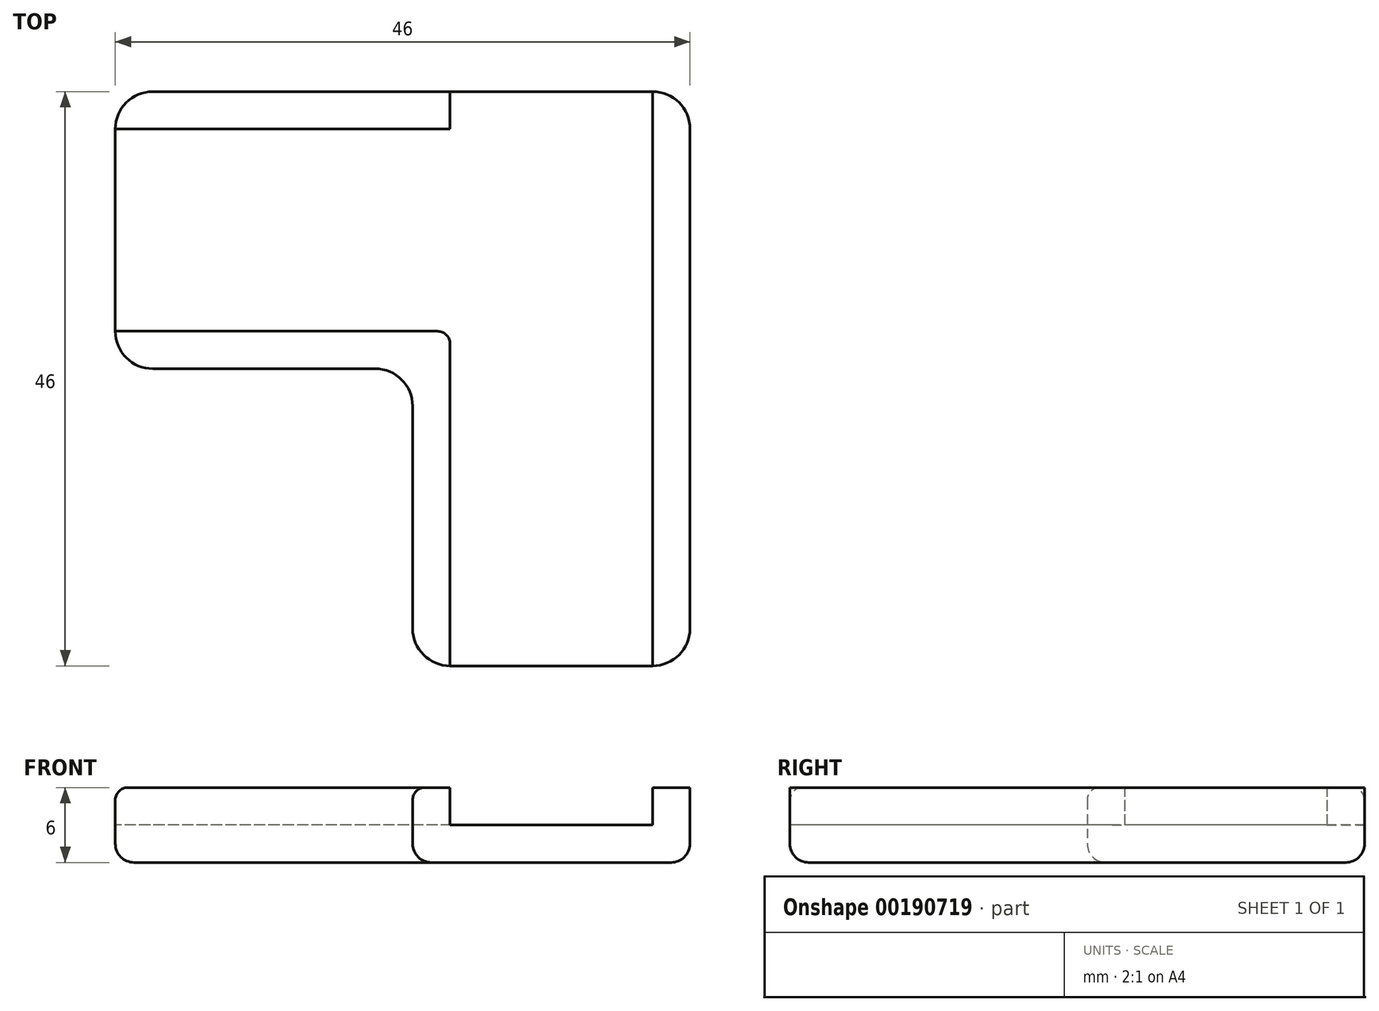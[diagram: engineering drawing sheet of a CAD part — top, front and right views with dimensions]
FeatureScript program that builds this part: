
annotation { "Feature Type Name" : "Feature", "Feature Type Description" : "" }
export const myFeature = defineFeature(function(context is Context, id is Id, definition is map)
    precondition{}
    {
        {
            var Q0;
            Q0=qCreatedBy(makeId("Top.planeOp"),FACE);
            var sketch = newSketch(context, id + "F0", { "sketchPlane" : qUnion([Q0])});
            skLineSegment(sketch, "E0.bottom", {"start": v(0, 0) * mm, "end": v(-40, 0) * mm, "construction": true});
            skLineSegment(sketch, "E0.top", {"start": v(-16.2, -16.2) * mm, "end": v(-40, -16.2) * mm, "construction": true});
            skLineSegment(sketch, "E0.left", {"start": v(0, 0) * mm, "end": v(0, -16.2) * mm, "construction": true});
            skLineSegment(sketch, "E0.right", {"start": v(-40, 0) * mm, "end": v(-40, -16.2) * mm, "construction": true});
            skLineSegment(sketch, "E1.bottom", {"start": v(0, 0) * mm, "end": v(-16.2, 0) * mm, "construction": true});
            skLineSegment(sketch, "E1.top", {"start": v(0, -40) * mm, "end": v(-16.2, -40) * mm, "construction": true});
            skLineSegment(sketch, "E1.left", {"start": v(0, 0) * mm, "end": v(0, -40) * mm, "construction": true});
            skLineSegment(sketch, "E1.right", {"start": v(-16.2, -16.2) * mm, "end": v(-16.2, -40) * mm, "construction": true});
            skLineSegment(sketch, "E2.0", {"start": v(3, 0) * mm, "end": v(3, -40) * mm});
            skLineSegment(sketch, "E2.1", {"start": v(-43, 0) * mm, "end": v(-43, -16.2) * mm});
            skLineSegment(sketch, "E2.2", {"start": v(-22.2, -19.2) * mm, "end": v(-40, -19.2) * mm});
            skLineSegment(sketch, "E2.3", {"start": v(0, 3) * mm, "end": v(-40, 3) * mm});
            skLineSegment(sketch, "E2.4", {"start": v(-19.2, -22.2) * mm, "end": v(-19.2, -40) * mm});
            skLineSegment(sketch, "E2.5", {"start": v(0, -43) * mm, "end": v(-16.2, -43) * mm});
            skPoint(sketch, "E3.visualSharp", {"position": v(-43, 3) * mm});
            skArc(sketch, "E3.filletArc", {"start": v(-40, 3) * mm, "mid": v(-42.12, 2.12) * mm, "end": v(-43, 0) * mm});
            skPoint(sketch, "E4.visualSharp", {"position": v(3, 3) * mm});
            skArc(sketch, "E4.filletArc", {"start": v(3, 0) * mm, "mid": v(2.12, 2.12) * mm, "end": v(0, 3) * mm});
            skPoint(sketch, "E5.visualSharp", {"position": v(3, -43) * mm});
            skArc(sketch, "E5.filletArc", {"start": v(0, -43) * mm, "mid": v(2.12, -42.12) * mm, "end": v(3, -40) * mm});
            skPoint(sketch, "E6.visualSharp", {"position": v(-19.2, -43) * mm});
            skArc(sketch, "E6.filletArc", {"start": v(-19.2, -40) * mm, "mid": v(-18.32, -42.12) * mm, "end": v(-16.2, -43) * mm});
            skPoint(sketch, "E7.visualSharp", {"position": v(-43, -19.2) * mm});
            skArc(sketch, "E7.filletArc", {"start": v(-43, -16.2) * mm, "mid": v(-42.12, -18.32) * mm, "end": v(-40, -19.2) * mm});
            skPoint(sketch, "E8.visualSharp", {"position": v(-19.2, -19.2) * mm});
            skArc(sketch, "E8.filletArc", {"start": v(-19.2, -22.2) * mm, "mid": v(-20.08, -20.08) * mm, "end": v(-22.2, -19.2) * mm});
            skSolve(sketch);
        }
        {
            var Q0;
            Q0=makeQuery(id+"F0.imprint","IMPRINT",FACE,{"disambiguationData":[TD([[makeQuery(id+"F0.imprint","IMPRINT",EDGE,{"derivedFrom":sQuery(id+"F0.wireOp",EDGE,"E2.0")}),-1.0]])]});
            extrude(context, id + "F1", {"entities" : qUnion([Q0]), "depth" : 6 * mm, "symmetric" : true});
        }
        {
            var Q0;
            Q0=qCreatedBy(makeId("Top.planeOp"),FACE);
            var sketch = newSketch(context, id + "F2", { "sketchPlane" : qUnion([Q0])});
            skLineSegment(sketch, "E9.0", {"start": v(-16.2, 0) * mm, "end": v(-43, 0) * mm});
            skLineSegment(sketch, "E9.1", {"start": v(-16.2, -16.2) * mm, "end": v(-43, -16.2) * mm});
            skLineSegment(sketch, "E9.2", {"start": v(0, 0) * mm, "end": v(0, -16.2) * mm});
            skLineSegment(sketch, "E9.6", {"start": v(0, 3) * mm, "end": v(0, -43) * mm});
            skLineSegment(sketch, "E9.7", {"start": v(-16.2, -16.2) * mm, "end": v(-16.2, -43) * mm});
            skLineSegment(sketch, "E9.9", {"start": v(-43, 0) * mm, "end": v(-43, -16.2) * mm});
            skLineSegment(sketch, "E9.10", {"start": v(-22.2, -19.2) * mm, "end": v(-40, -19.2) * mm});
            skPoint(sketch, "E9.11.end.orphan", {"position": v(-40, 3) * mm});
            skPoint(sketch, "E9.11.start.orphan", {"position": v(0, 3) * mm});
            skPoint(sketch, "E9.8.end.orphan", {"position": v(3, -40) * mm});
            skPoint(sketch, "E9.8.start.orphan", {"position": v(3, 0) * mm});
            skPoint(sketch, "E9.13.end.orphan", {"position": v(-16.2, -43) * mm});
            skPoint(sketch, "E9.13.start.orphan", {"position": v(0, -43) * mm});
            skPoint(sketch, "E9.12.end.orphan", {"position": v(-19.2, -40) * mm});
            skPoint(sketch, "E9.12.start.orphan", {"position": v(-19.2, -22.2) * mm});
            skPoint(sketch, "E9.3.end.orphan", {"position": v(-40, -16.2) * mm});
            skPoint(sketch, "E9.3.start.orphan", {"position": v(-40, 0) * mm});
            skPoint(sketch, "E9.5.end.orphan", {"position": v(-16.2, -40) * mm});
            skPoint(sketch, "E9.5.start.orphan", {"position": v(0, -40) * mm});
            skLineSegment(sketch, "E10.0", {"start": v(0, -43) * mm, "end": v(-16.2, -43) * mm, "construction": true});
            skPoint(sketch, "E11.orphan", {"position": v(-43, 0) * mm});
            skPoint(sketch, "E12.orphan", {"position": v(-43, -16.2) * mm});
            skLineSegment(sketch, "E13", {"start": v(-16.2, -43) * mm, "end": v(0, -43) * mm});
            skPoint(sketch, "E9.4.end.orphan", {"position": v(-16.2, 0) * mm});
            skPoint(sketch, "E9.4.start.orphan", {"position": v(0, 0) * mm});
            skLineSegment(sketch, "E14", {"start": v(-16.2, 0) * mm, "end": v(-16.2, 3) * mm});
            skLineSegment(sketch, "E15", {"start": v(0, 3) * mm, "end": v(-16.2, 3) * mm});
            skSolve(sketch);
        }
        {
            var Q0;
            Q0 = qSketchRegion(id + "F2", true);
            extrude(context, id + "F3", {"entities" : qUnion([Q0]), "operationType" : NewBodyOperationType.REMOVE, "depth" : 4 * mm});
        }
        {
            var Q0;
            Q0=makeQuery(id+"F1.opExtrude","CAP_FACE",FACE,{"disambiguationData":[OSD([sQuery(id+"F0.wireOp",EDGE,"E2.0"),sQuery(id+"F0.wireOp",EDGE,"E2.1"),sQuery(id+"F0.wireOp",EDGE,"E2.2"),sQuery(id+"F0.wireOp",EDGE,"E2.3"),sQuery(id+"F0.wireOp",EDGE,"E2.4"),sQuery(id+"F0.wireOp",EDGE,"E2.5"),sQuery(id+"F0.wireOp",EDGE,"E3.filletArc"),sQuery(id+"F0.wireOp",EDGE,"E4.filletArc"),sQuery(id+"F0.wireOp",EDGE,"E5.filletArc"),sQuery(id+"F0.wireOp",EDGE,"E6.filletArc"),sQuery(id+"F0.wireOp",EDGE,"E7.filletArc"),sQuery(id+"F0.wireOp",EDGE,"E8.filletArc")])],"isStart":true});
            fillet(context, id + "F4", {"entities" : qUnion([Q0]), "radius" : 1.5 * mm, "tangentPropagation" : true, "allowEdgeOverflow" : false});
        }
        {
            var Q0;
            Q0=makeQuery(id+"F1.opExtrude","CAP_EDGE",EDGE,{"disambiguationData":[OSD([sQuery(id+"F0.wireOp",EDGE,"E2.3")])],"isStart":false});
            var Q1;
            Q1=makeQuery(id+"F1.opExtrude","CAP_EDGE",EDGE,{"disambiguationData":[OSD([sQuery(id+"F0.wireOp",EDGE,"E2.4")])],"isStart":false});
            var Q2;
            Q2=makeQuery(id+"F3.boolean.opBoolean","COPY",EDGE,{"derivedFrom":makeQuery(id+"F3.opExtrude","SWEPT_EDGE",EDGE,{"disambiguationData":[OSD([sQuery(id+"F2.wireOp",EDGE,"E9.1"),sQuery(id+"F2.wireOp",EDGE,"E9.7")])]})});
            fillet(context, id + "F5", {"entities" : qUnion([Q0, Q1, Q2]), "radius" : 1 * mm, "tangentPropagation" : true, "allowEdgeOverflow" : false});
        }
    });
